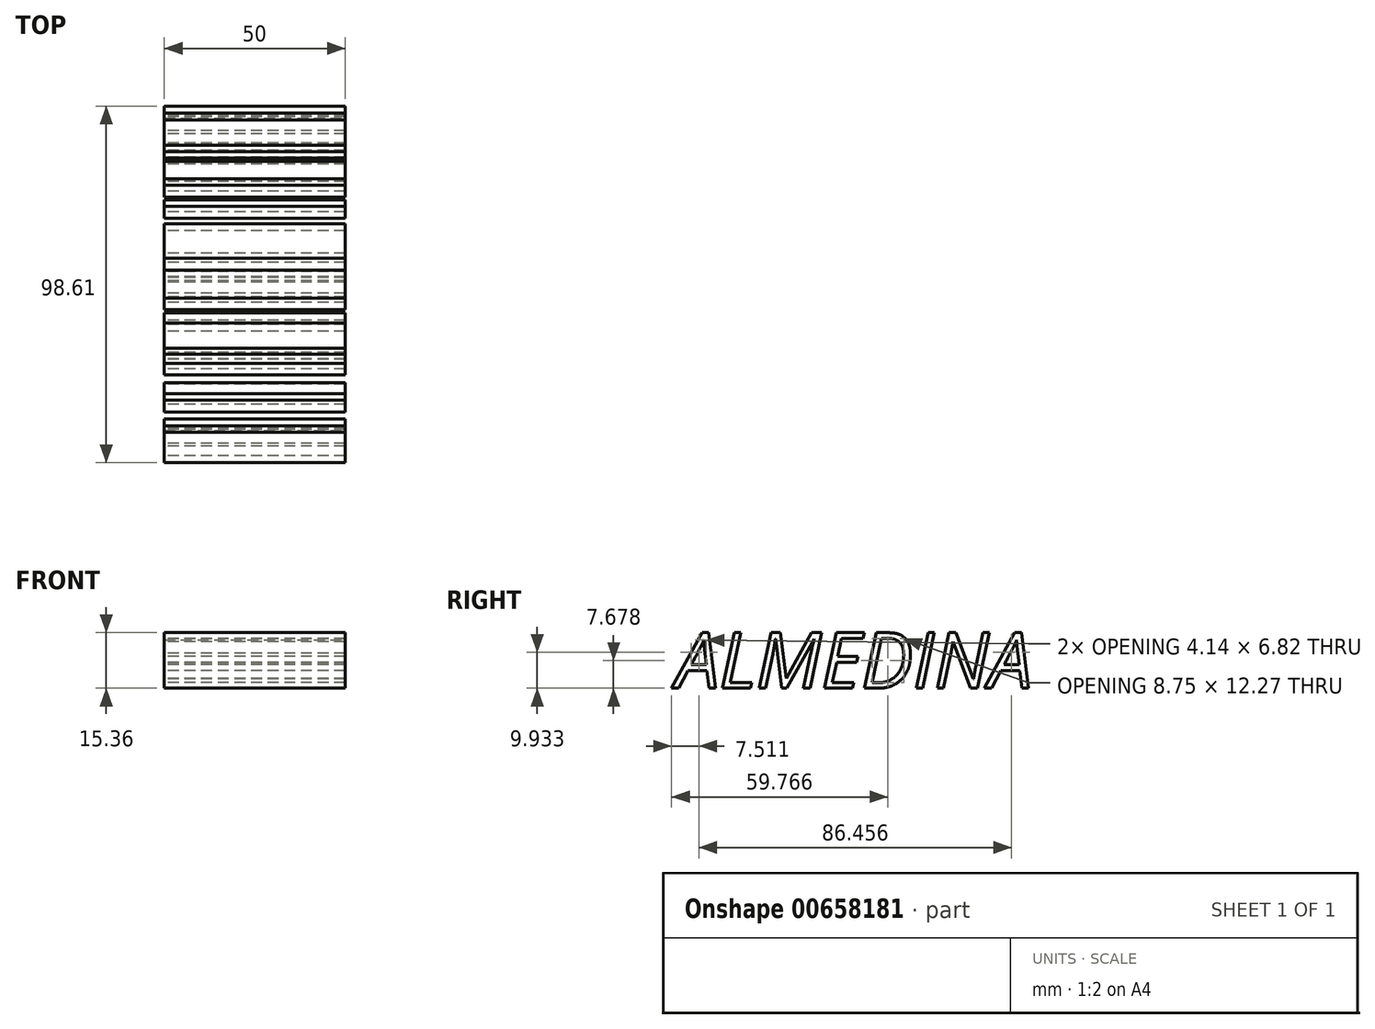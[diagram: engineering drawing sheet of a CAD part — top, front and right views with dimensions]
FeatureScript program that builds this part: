
annotation { "Feature Type Name" : "Feature", "Feature Type Description" : "" }
export const myFeature = defineFeature(function(context is Context, id is Id, definition is map)
    precondition{}
    {
        {
            var Q0;
            Q0=qCreatedBy(makeId("Right.planeOp"),FACE);
            var sketch = newSketch(context, id + "F0", { "sketchPlane" : qUnion([Q0])});
            skText(sketch, "E0", { "text": "ALMEDINA", "fontName": "OpenSans-Italic.ttf"});
            const initialGuessF0  = {"E0": [-0.03564, 0.0132, 1, 0, 0.01549]};
            skSetInitialGuess(sketch, initialGuessF0);
            skSolve(sketch);
        }
        {
            var Q0;
            Q0=qSketchRegion(id+"F0",true);
            extrude(context, id + "F1", {"entities" : qUnion([Q0]), "endBound" : BoundingType.SYMMETRIC, "depth" : 50 * mm, "offsetDistance" : 25 * mm});
        }
    });
